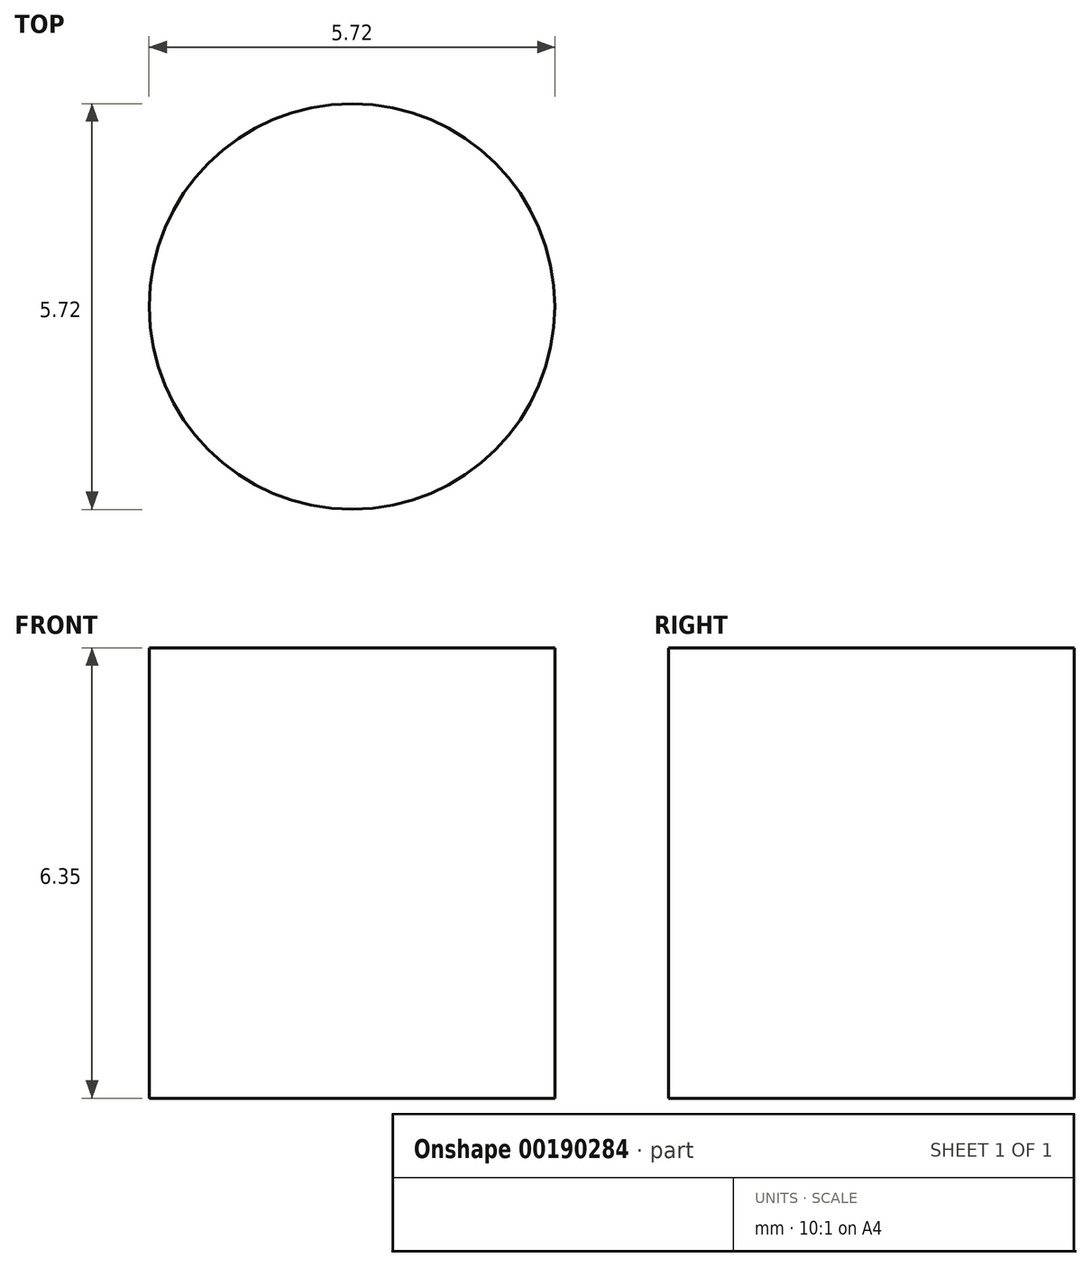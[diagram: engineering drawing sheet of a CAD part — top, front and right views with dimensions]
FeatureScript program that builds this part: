
annotation { "Feature Type Name" : "Feature", "Feature Type Description" : "" }
export const myFeature = defineFeature(function(context is Context, id is Id, definition is map)
    precondition{}
    {
        {
            var Q0;
            Q0=qCreatedBy(makeId("Top.planeOp"),FACE);
            var sketch = newSketch(context, id + "F0", { "sketchPlane" : qUnion([Q0])});
            skCircle(sketch, "E0", {"center": v(0, 0) * mm, "radius": 2.86 * mm});
            skSolve(sketch);
        }
        {
            var Q0;
            Q0 = qSketchRegion(id + "F0", true);
            extrude(context, id + "F1", {"entities" : qUnion([Q0]), "depth" : 6.35 * mm});
        }
    });
